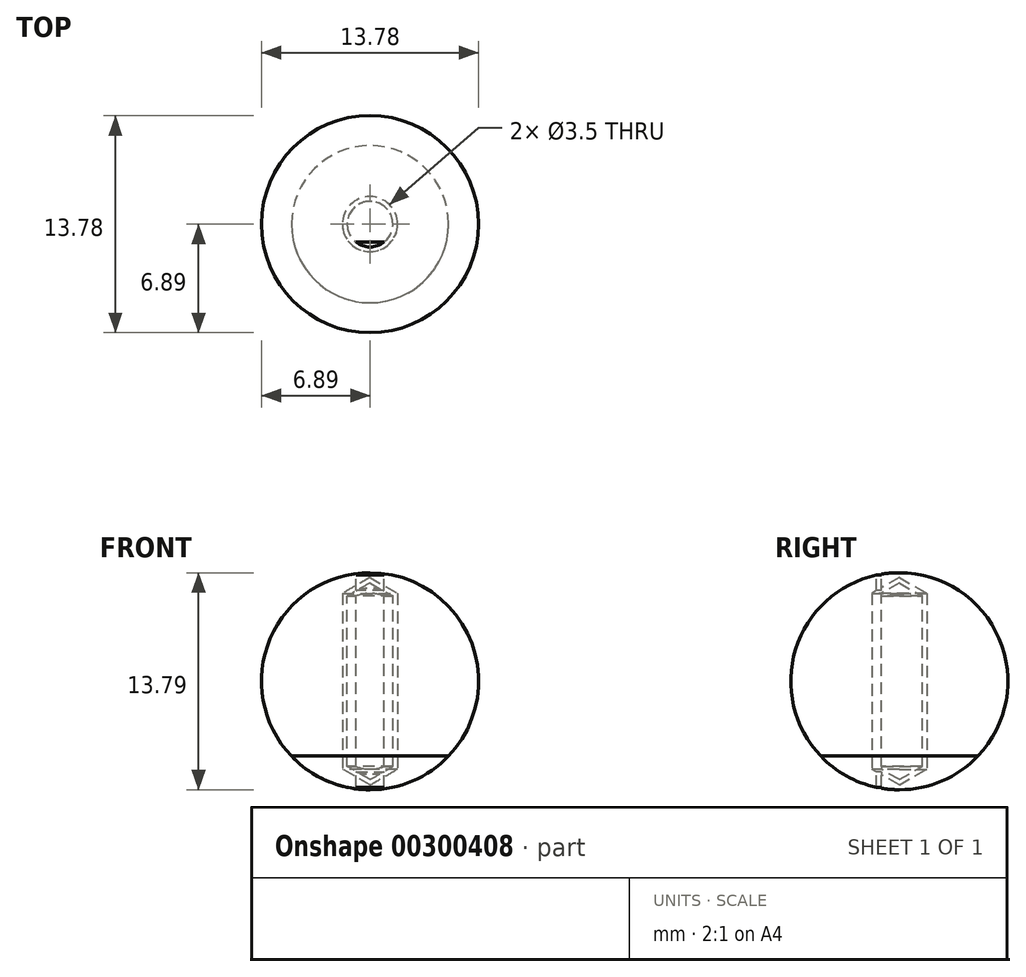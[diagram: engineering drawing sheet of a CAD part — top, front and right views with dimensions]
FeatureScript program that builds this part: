
annotation { "Feature Type Name" : "Feature", "Feature Type Description" : "" }
export const myFeature = defineFeature(function(context is Context, id is Id, definition is map)
    precondition{}
    {
        {
            var Q0;
            Q0=qCreatedBy(makeId("Front.planeOp"),FACE);
            var sketch = newSketch(context, id + "F0", { "sketchPlane" : qUnion([Q0])});
            skLineSegment(sketch, "E0", {"start": v(4.99, 0) * mm, "end": v(1.75, 0) * mm});
            skLineSegment(sketch, "E1", {"start": v(0, 0) * mm, "end": v(0, -2.5) * mm, "construction": true});
            skLineSegment(sketch, "E2", {"start": v(0, -2.5) * mm, "end": v(0, 11.35) * mm, "construction": true});
            skLineSegment(sketch, "E3", {"start": v(0, 11.35) * mm, "end": v(0, 0) * mm, "construction": true});
            skLineSegment(sketch, "E4", {"start": v(1.75, 0) * mm, "end": v(1.75, 10.34) * mm});
            skLineSegment(sketch, "E5", {"start": v(1.75, 10.34) * mm, "end": v(0, 11.35) * mm});
            skLineSegment(sketch, "E6", {"start": v(0, 0) * mm, "end": v(1.75, 0) * mm, "construction": true});
            skLineSegment(sketch, "E7", {"start": v(0, 11.35) * mm, "end": v(0, 11.65) * mm});
            skArc(sketch, "E8", {"start": v(4.99, 0) * mm, "mid": v(6.34, 7.47) * mm, "end": v(0, 11.65) * mm});
            skArc(sketch, "E9", {"start": v(0, -2.14) * mm, "mid": v(2.71, -1.58) * mm, "end": v(4.99, 0) * mm});
            skLineSegment(sketch, "E10", {"start": v(0, -2.14) * mm, "end": v(0, -1.84) * mm});
            skLineSegment(sketch, "E11", {"start": v(0, -1.84) * mm, "end": v(1.75, -0.83) * mm});
            skLineSegment(sketch, "E12", {"start": v(1.75, 0) * mm, "end": v(1.75, -0.83) * mm});
            skLineSegment(sketch, "E13", {"start": v(0, -1.84) * mm, "end": v(0, 11.35) * mm, "construction": true});
            skLineSegment(sketch, "E14.0", {"start": v(1.45, 0) * mm, "end": v(1.45, -0.65) * mm});
            skLineSegment(sketch, "E14.1", {"start": v(0, -1.5) * mm, "end": v(1.45, -0.65) * mm});
            skLineSegment(sketch, "E14.2", {"start": v(1.45, 0) * mm, "end": v(1.45, 10.17) * mm});
            skLineSegment(sketch, "E14.3", {"start": v(1.45, 10.17) * mm, "end": v(0, 11) * mm});
            skLineSegment(sketch, "E15", {"start": v(0, 11) * mm, "end": v(0, -1.5) * mm});
            skSolve(sketch);
        }
        {
            var Q0;
            Q0=makeQuery(id+"F0.imprint","IMPRINT",FACE,{"disambiguationData":[TD([[makeQuery(id+"F0.imprint","IMPRINT",EDGE,{"derivedFrom":sQuery(id+"F0.wireOp",EDGE,"E0")}),-1.0]])]});
            var Q1;
            Q1=sQuery(id+"F0.wireOp",EDGE,"E2");
            revolve(context, id + "F1", {"entities" : qUnion([Q0]), "axis" : qUnion([Q1]), "revolveType" : RevolveType.FULL});
        }
        {
            var Q0;
            Q0=makeQuery(id+"F0.imprint","IMPRINT",FACE,{"disambiguationData":[TD([[makeQuery(id+"F0.imprint","IMPRINT",EDGE,{"derivedFrom":sQuery(id+"F0.wireOp",EDGE,"E0")}),1.0]])]});
            var Q1;
            Q1=sQuery(id+"F0.wireOp",EDGE,"E2");
            revolve(context, id + "F2", {"entities" : qUnion([Q0]), "axis" : qUnion([Q1]), "revolveType" : RevolveType.FULL});
        }
        {
            var Q0;
            Q0=makeQuery(id+"F0.imprint","IMPRINT",FACE,{"disambiguationData":[TD([[makeQuery(id+"F0.imprint","IMPRINT",EDGE,{"derivedFrom":sQuery(id+"F0.wireOp",EDGE,"E14.0")}),-1.0]])]});
            var Q1;
            Q1=sQuery(id+"F0.wireOp",EDGE,"E15");
            revolve(context, id + "F3", {"entities" : qUnion([Q0]), "axis" : qUnion([Q1]), "revolveType" : RevolveType.FULL});
        }
        {
            var Q0;
            Q0=qCreatedBy(makeId("Top.planeOp"),FACE);
            var sketch = newSketch(context, id + "F4", { "sketchPlane" : qUnion([Q0])});
            skCircle(sketch, "E16.0", {"center": v(0, 0) * mm, "radius": 1.45 * mm});
            skLineSegment(sketch, "E17", {"start": v(-0.9, -1.14) * mm, "end": v(0.9, -1.14) * mm});
            skSolve(sketch);
        }
        {
            var Q0;
            {var subQ0=sQuery(id+"F4.wireOp",EDGE,"E17");Q0=makeQuery(id+"F4.imprint","IMPRINT",FACE,{"disambiguationData":[TD([[makeQuery(id+"F4.imprint","IMPRINT",EDGE,{"derivedFrom":subQ0}),-1.0]])]});}
            extrude(context, id + "F5", {"entities" : qUnion([Q0]), "operationType" : NewBodyOperationType.REMOVE, "endBound" : BoundingType.THROUGH_ALL, "oppositeDirection" : true, "depth" : 25 * mm, "hasSecondDirection" : true, "secondDirectionBound" : SecondDirectionBoundingType.THROUGH_ALL, "secondDirectionOppositeDirection" : false, "secondDirectionDepth" : 25 * mm});
        }
    });
